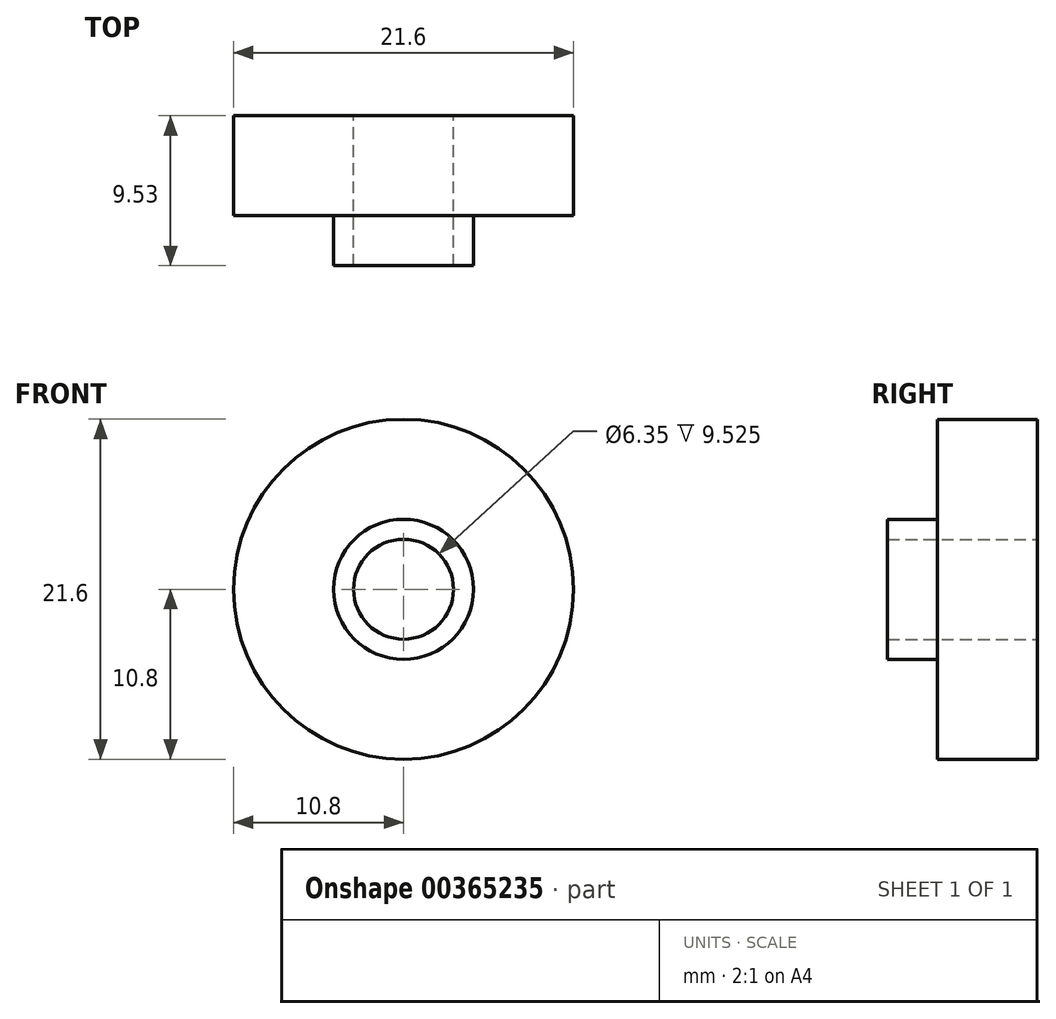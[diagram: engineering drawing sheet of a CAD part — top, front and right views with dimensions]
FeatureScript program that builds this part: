
annotation { "Feature Type Name" : "Feature", "Feature Type Description" : "" }
export const myFeature = defineFeature(function(context is Context, id is Id, definition is map)
    precondition{}
    {
        {
            var Q0;
            Q0=qCreatedBy(makeId("Right.planeOp"),FACE);
            var sketch = newSketch(context, id + "F0", { "sketchPlane" : qUnion([Q0])});
            skLineSegment(sketch, "E0", {"start": v(0, 0) * mm, "end": v(-22.7, 0) * mm, "construction": true});
            skLineSegment(sketch, "E1", {"start": v(0, 0) * mm, "end": v(0, 10.8) * mm});
            skLineSegment(sketch, "E2", {"start": v(0, 10.8) * mm, "end": v(-6.35, 10.8) * mm});
            skLineSegment(sketch, "E3", {"start": v(-6.35, 10.8) * mm, "end": v(-6.35, 4.45) * mm});
            skLineSegment(sketch, "E4", {"start": v(-6.35, 4.45) * mm, "end": v(-9.53, 4.45) * mm});
            skLineSegment(sketch, "E5", {"start": v(-9.53, 4.45) * mm, "end": v(-9.53, 3.17) * mm});
            skLineSegment(sketch, "E6", {"start": v(-9.53, 3.17) * mm, "end": v(0, 3.18) * mm});
            skSolve(sketch);
        }
        {
            var Q0;
            {var subQ0=sQuery(id+"F0.wireOp",EDGE,"E2");Q0=makeQuery(id+"F0.imprint","IMPRINT",FACE,{"disambiguationData":[TD([[makeQuery(id+"F0.imprint","IMPRINT",EDGE,{"derivedFrom":subQ0}),1.0]])]});}
            var Q1;
            Q1=sQuery(id+"F0.wireOp",EDGE,"E0");
            revolve(context, id + "F1", {"entities" : qUnion([Q0]), "axis" : qUnion([Q1]), "revolveType" : RevolveType.FULL});
        }
    });
